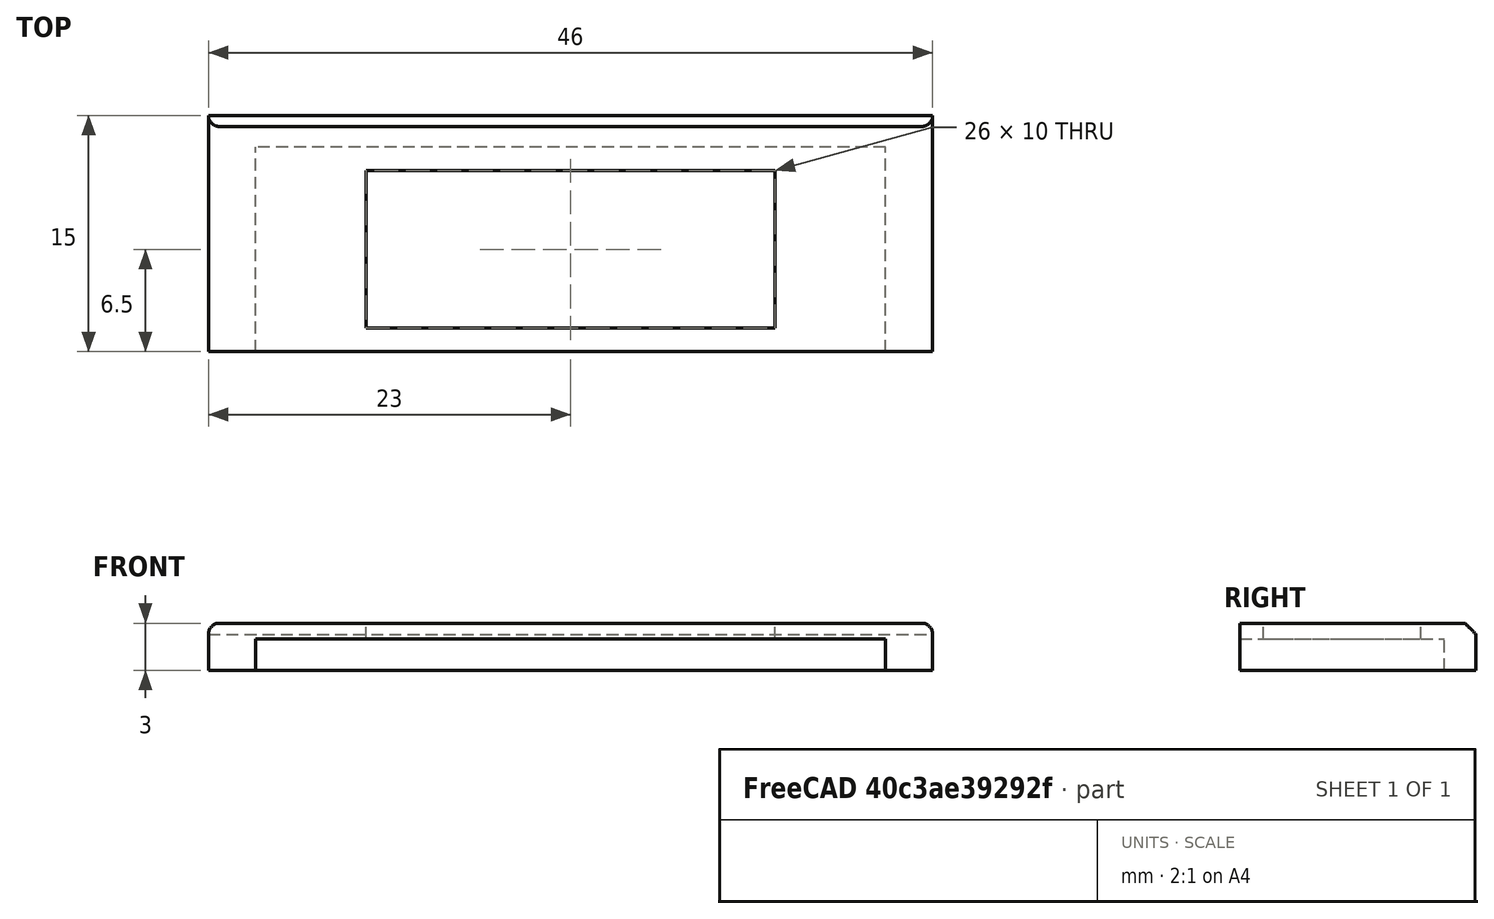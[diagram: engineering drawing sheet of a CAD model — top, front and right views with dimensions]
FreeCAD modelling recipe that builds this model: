
FCSTD DOCUMENT  (FreeCAD 0.20R29410 (Git))
Label: RTO_Cart_LCD
License: All rights reserved
LicenseURL: http://en.wikipedia.org/wiki/All_rights_reserved
objects: Part::Box×5, Part::Cut×3, Part::MultiFuse×1, Part::Chamfer×1, Part::Fillet×1, Mesh::Feature×1, Part::Feature×1
note: 12 computed .brp shape members not serialized (recipe doc carries the construction recipe); baked Part::Feature solids carry a one-line shape summary decoded from their .brp

FEATURE [Part::Box] Box  label="base"
  AttacherType = Attacher::AttachEngine3D
  Height = 2
  Length = 46
  Placement = pos=(-2,0,1) rot=(0,0,1;0rad)
  Width = 17
FEATURE [Part::Box] Box001  label="Foro1"
  AttacherType = Attacher::AttachEngine3D
  Height = 6
  Length = 40
  Placement = pos=(1,2,-3) rot=(0,0,1;0rad)
  Width = 13
FEATURE [Part::Cut] Cut
  Base = -> Box
  Tool = -> Box001
FEATURE [Part::Box] Box002  label="Cubo"
  AttacherType = Attacher::AttachEngine3D
  Height = 1
  Length = 46
  Placement = pos=(-2,0,3) rot=(0,0,1;0rad)
  Width = 17
FEATURE [Part::MultiFuse] Fusion
  Shapes = -> [Cut,Box002]
FEATURE [Part::Chamfer] Chamfer
  Base = -> Fusion
  Edges = 2 edges r=0.7: [Edge7,Edge8]
FEATURE [Part::Fillet] Fillet
  Base = -> Chamfer
  Edges = 2 edges r=0.7: [Edge5,Edge15]
FEATURE [Part::Box] Box003  label="Cubo001"
  AttacherType = Attacher::AttachEngine3D
  Height = 5
  Length = 26
  Placement = pos=(8,3.5,0) rot=(0,0,1;0rad)
  Width = 10
FEATURE [Part::Cut] Cut001
  Base = -> Fillet
  Tool = -> Box003
FEATURE [Part::Box] Box004  label="Cubo002"
  AttacherType = Attacher::AttachEngine3D
  Height = 10
  Length = 48
  Placement = pos=(-3,-3,-1) rot=(0,0,1;0rad)
  Width = 5
FEATURE [Part::Cut] Cut002
  Base = -> Cut001
  Tool = -> Box004
FEATURE [Mesh::Feature] Mesh  label="Cut002 (Meshed)"
FEATURE [Part::Feature] Refined_Mesh_Solid_99120
  shape: bbox 46 x 15 x 3 mm, 57 faces, 0 solids (baked)
